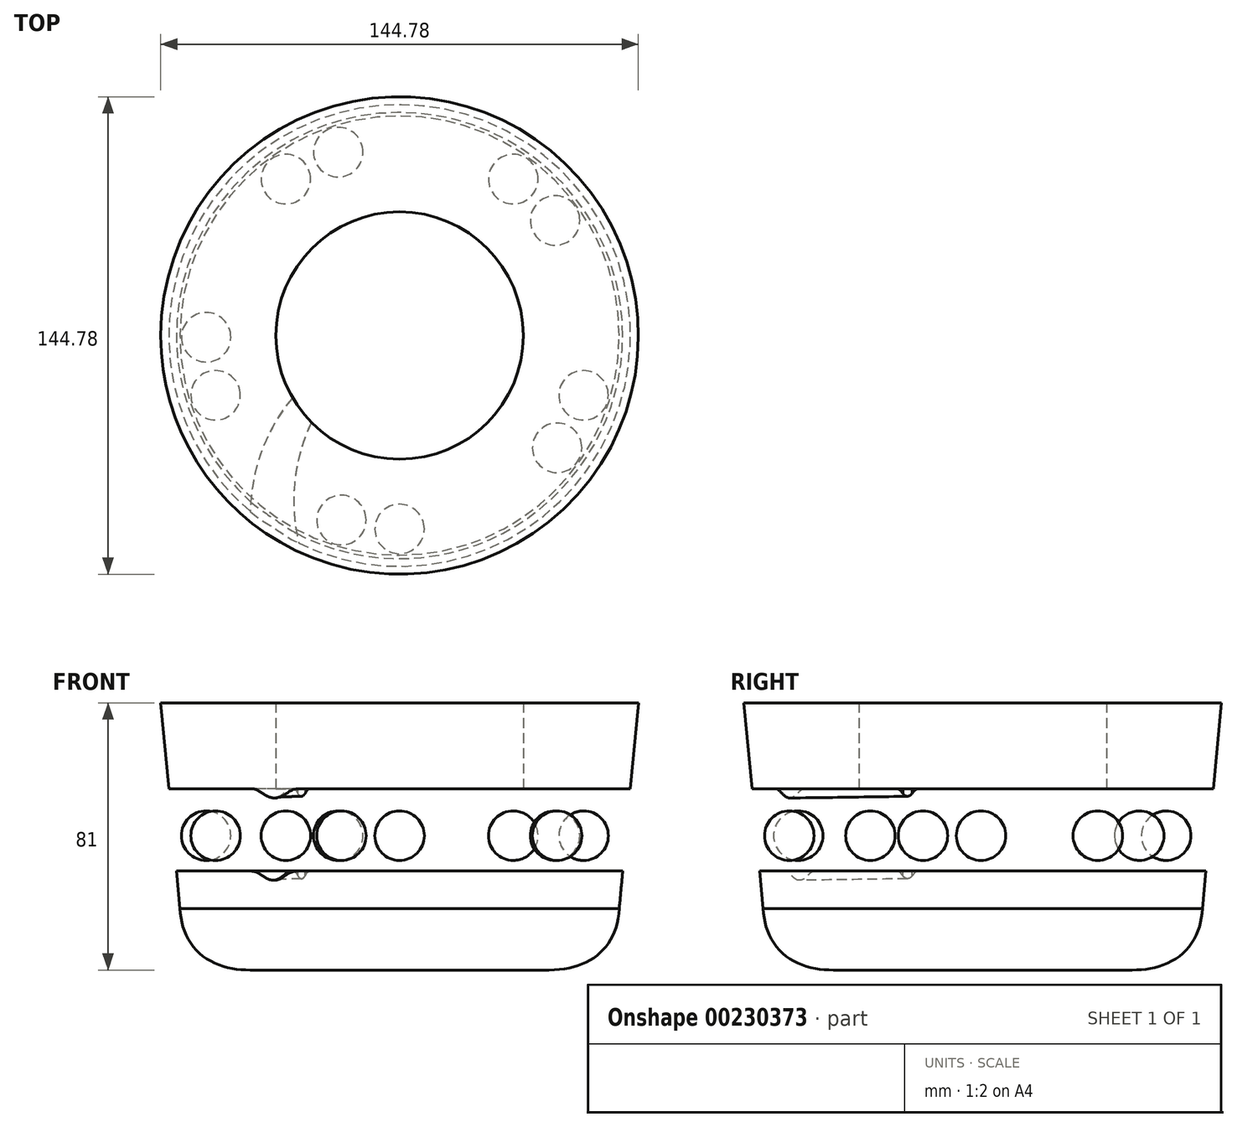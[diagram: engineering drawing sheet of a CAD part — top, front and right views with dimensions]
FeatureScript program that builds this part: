
annotation { "Feature Type Name" : "Feature", "Feature Type Description" : "" }
export const myFeature = defineFeature(function(context is Context, id is Id, definition is map)
    precondition{}
    {
        {
            var Q0;
            Q0=qCreatedBy(makeId("Top.planeOp"),FACE);
            var sketch = newSketch(context, id + "F0", { "sketchPlane" : qUnion([Q0])});
            skCircle(sketch, "E0", {"center": v(0, 0) * mm, "radius": 75 * mm});
            skSolve(sketch);
        }
        {
            var Q0;
            Q0 = qSketchRegion(id + "F0", true);
            extrude(context, id + "F1", {"entities" : qUnion([Q0]), "depth" : 30 * mm, "offsetDistance" : 25 * mm});
        }
        {
            var Q0;
            Q0=makeQuery(id+"F1.opExtrude","CAP_FACE",FACE,{"disambiguationData":[OSD([sQuery(id+"F0.wireOp",EDGE,"E0")])],"isStart":false});
            var sketch = newSketch(context, id + "F2", { "sketchPlane" : qUnion([Q0])});
            skCircle(sketch, "E1", {"center": v(0, 0) * mm, "radius": 37.5 * mm});
            skSolve(sketch);
        }
        {
            var Q0;
            Q0=makeQuery(id+"F2.imprint","IMPRINT",FACE,{"disambiguationData":[TD([[makeQuery(id+"F2.imprint","IMPRINT",EDGE,{"derivedFrom":sQuery(id+"F2.wireOp",EDGE,"E1")}),1.0]])]});
            extrude(context, id + "F3", {"entities" : qUnion([Q0]), "operationType" : NewBodyOperationType.REMOVE, "oppositeDirection" : true, "depth" : 30 * mm, "offsetDistance" : 25 * mm});
        }
        {
            var Q0;
            Q0=makeQuery(id+"F1.opExtrude","CAP_FACE",FACE,{"disambiguationData":[OSD([sQuery(id+"F0.wireOp",EDGE,"E0")])],"isStart":false});
            var sketch = newSketch(context, id + "F4", { "sketchPlane" : qUnion([Q0])});
            skCircle(sketch, "E2", {"center": v(0, 0) * mm, "radius": 100 * mm});
            skCircle(sketch, "E3", {"center": v(0, 0) * mm, "radius": 37.75 * mm});
            skArc(sketch, "E4", {"start": v(-26.84, -26.55) * mm, "mid": v(-28.75, -68.88) * mm, "end": v(0, -100) * mm});
            skPoint(sketch, "E5", {"position": v(-26.84, -26.55) * mm});
            skArc(sketch, "E6.1.0", {"start": v(0, 0) * mm, "mid": v(-18.64, -56.4) * mm, "end": v(24.87, -96.86) * mm});
            skArc(sketch, "E6.2.0", {"start": v(0, 0) * mm, "mid": v(-4.03, -59.27) * mm, "end": v(48.18, -87.63) * mm});
            skArc(sketch, "E6.3.0", {"start": v(0, 0) * mm, "mid": v(10.84, -58.41) * mm, "end": v(68.45, -72.9) * mm});
            skArc(sketch, "E6.4.0", {"start": v(0, 0) * mm, "mid": v(25.02, -53.88) * mm, "end": v(84.43, -53.58) * mm});
            skArc(sketch, "E6.5.0", {"start": v(0, 0) * mm, "mid": v(37.64, -45.97) * mm, "end": v(95.1, -30.9) * mm});
            skArc(sketch, "E6.6.0", {"start": v(0, 0) * mm, "mid": v(47.89, -35.16) * mm, "end": v(99.8, -6.28) * mm});
            skArc(sketch, "E6.7.0", {"start": v(0, 0) * mm, "mid": v(55.13, -22.15) * mm, "end": v(98.23, 18.74) * mm});
            skArc(sketch, "E6.8.0", {"start": v(0, 0) * mm, "mid": v(58.9, -7.74) * mm, "end": v(90.48, 42.58) * mm});
            skArc(sketch, "E6.9.0", {"start": v(0, 0) * mm, "mid": v(58.98, 7.15) * mm, "end": v(77.05, 63.74) * mm});
            skArc(sketch, "E6.10.0", {"start": v(0, 0) * mm, "mid": v(55.35, 21.6) * mm, "end": v(58.78, 80.9) * mm});
            skArc(sketch, "E6.11.0", {"start": v(0, 0) * mm, "mid": v(48.24, 34.68) * mm, "end": v(36.81, 92.98) * mm});
            skArc(sketch, "E6.12.0", {"start": v(0, 0) * mm, "mid": v(38.1, 45.58) * mm, "end": v(12.53, 99.21) * mm});
            skArc(sketch, "E6.13.0", {"start": v(0, 0) * mm, "mid": v(25.57, 53.63) * mm, "end": v(-12.53, 99.21) * mm});
            skArc(sketch, "E6.14.0", {"start": v(0, 0) * mm, "mid": v(11.43, 58.3) * mm, "end": v(-36.81, 92.98) * mm});
            skArc(sketch, "E6.15.0", {"start": v(0, 0) * mm, "mid": v(-3.43, 59.31) * mm, "end": v(-58.78, 80.9) * mm});
            skArc(sketch, "E6.16.0", {"start": v(0, 0) * mm, "mid": v(-18.07, 56.6) * mm, "end": v(-77.05, 63.74) * mm});
            skArc(sketch, "E6.17.0", {"start": v(0, 0) * mm, "mid": v(-31.58, 50.32) * mm, "end": v(-90.48, 42.58) * mm});
            skArc(sketch, "E6.18.0", {"start": v(0, 0) * mm, "mid": v(-43.1, 40.89) * mm, "end": v(-98.23, 18.74) * mm});
            skArc(sketch, "E6.19.0", {"start": v(0, 0) * mm, "mid": v(-51.92, 28.88) * mm, "end": v(-99.8, -6.28) * mm});
            skArc(sketch, "E6.20.0", {"start": v(0, 0) * mm, "mid": v(-57.47, 15.07) * mm, "end": v(-95.1, -30.9) * mm});
            skArc(sketch, "E6.21.0", {"start": v(0, 0) * mm, "mid": v(-59.4, 0.3) * mm, "end": v(-84.43, -53.58) * mm});
            skArc(sketch, "E6.22.0", {"start": v(0, 0) * mm, "mid": v(-57.62, -14.48) * mm, "end": v(-68.45, -72.9) * mm});
            skArc(sketch, "E6.23.0", {"start": v(0, 0) * mm, "mid": v(-52.2, -28.36) * mm, "end": v(-48.18, -87.63) * mm});
            skArc(sketch, "E6.24.0", {"start": v(-32.6, -19.04) * mm, "mid": v(-44.97, -59.56) * mm, "end": v(-24.87, -96.86) * mm});
            skLineSegment(sketch, "E7", {"start": v(0, -100) * mm, "end": v(-24.87, -96.86) * mm});
            skPoint(sketch, "E8", {"position": v(-32.6, -19.04) * mm});
            skLineSegment(sketch, "E9", {"start": v(-32.6, -19.04) * mm, "end": v(-26.84, -26.55) * mm});
            skPoint(sketch, "E10", {"position": v(-29.72, -22.8) * mm});
            skSolve(sketch);
        }
        {
            var Q0;
            Q0=makeQuery(id+"F1.opExtrude","SWEPT_BODY",BODY,{"disambiguationData":[OSD([sQuery(id+"F0.wireOp",EDGE,"E0")])]});
            var Q1;
            Q1=qCreatedBy(makeId("Top.planeOp"),FACE);
            mirror(context, id + "F5", {"entities" : qUnion([Q0]), "mirrorPlane" : qUnion([Q1])});
        }
        {
            var Q0;
            Q0=sQuery(id+"F4.wireOp",EDGE,"E7");
            cPlane(context, id + "F6", {"entities" : qUnion([Q0]), "cplaneType" : CPlaneType.LINE_ANGLE, "offset" : 25 * mm, "angle" : 0 * degree, "width" : 150 * mm, "height" : 150 * mm});
        }
        {
            var Q0;
            Q0=qCreatedBy(id+"F6.planeOp",FACE);
            var sketch = newSketch(context, id + "F7", { "sketchPlane" : qUnion([Q0])});
            skPoint(sketch, "E11.0", {"position": v(-12.53, 30) * mm});
            skPoint(sketch, "E12.0", {"position": v(12.53, 30) * mm});
            skPoint(sketch, "E13.0", {"position": v(0, 30) * mm});
            skFitSpline(sketch, "E14", {"points": [v(-12.53, 30) * mm, v(-5.15, 27.51) * mm, v(0, 26.47) * mm, v(5.15, 27.51) * mm, v(12.53, 30) * mm], "startDerivative": vector(33.53, 0) * mm, "endDerivative": vector(33.53, 0) * mm});
            skLineSegment(sketch, "E15", {"start": v(-12.53, 30) * mm, "end": v(12.53, 30) * mm});
            skLineSegment(sketch, "E16", {"start": v(0, 30) * mm, "end": v(0, 26.47) * mm, "construction": true});
            skSolve(sketch);
        }
        {
            var Q0;
            Q0=sQuery(id+"F4.wireOp",EDGE,"E9");
            cPlane(context, id + "F8", {"entities" : qUnion([Q0]), "cplaneType" : CPlaneType.LINE_ANGLE, "offset" : 25 * mm, "angle" : 90 * degree, "width" : 150 * mm, "height" : 150 * mm});
        }
        {
            var Q0;
            Q0=qCreatedBy(id+"F8.planeOp",FACE);
            var sketch = newSketch(context, id + "F9", { "sketchPlane" : qUnion([Q0])});
            skPoint(sketch, "E17.0", {"position": v(4.73, 30) * mm});
            skPoint(sketch, "E18.0", {"position": v(0, 30) * mm});
            skPoint(sketch, "E19.0", {"position": v(-4.73, 30) * mm});
            skFitSpline(sketch, "E20", {"points": [v(4.73, 30) * mm, v(2.06, 28.8) * mm, v(0, 27.68) * mm, v(-2.06, 28.8) * mm, v(-4.73, 30) * mm], "startDerivative": vector(-21.02, 0) * mm, "endDerivative": vector(-21.02, 0) * mm});
            skLineSegment(sketch, "E21", {"start": v(4.73, 30) * mm, "end": v(-4.73, 30) * mm});
            skLineSegment(sketch, "E22", {"start": v(0, 30) * mm, "end": v(0, 27.68) * mm, "construction": true});
            skSolve(sketch);
        }
        {
            var Q1;
            Q1 = qSketchRegion(id + "F7", true);
            var Q2;
            Q2 = qSketchRegion(id + "F9", true);
            var Q3;
            Q3=sQuery(id+"F4.wireOp",EDGE,"E6.24.0");
            var Q4;
            Q4=sQuery(id+"F4.wireOp",EDGE,"E4");
            loft(context, id + "F10", {"operationType" : NewBodyOperationType.REMOVE, "addGuides" : true, "sheetProfilesArray" : [{ "sheetProfileEntities" : qUnion([Q1]) }, { "sheetProfileEntities" : qUnion([Q2]) }], "guidesArray" : [{ "guideEntities" : qUnion([Q3]), "guideDerivativeType" : LoftGuideDerivativeType.DEFAULT, "guideDerivativeMagnitude" : 1 }, { "guideEntities" : qUnion([Q4]), "guideDerivativeType" : LoftGuideDerivativeType.DEFAULT, "guideDerivativeMagnitude" : 1 }]});
        }
        {
            var Q0;
            Q0=makeQuery(id+"F5.opPattern","COPY",BODY,{"derivedFrom":makeQuery(id+"F1.opExtrude","SWEPT_BODY",BODY,{"disambiguationData":[OSD([sQuery(id+"F0.wireOp",EDGE,"E0")])]}),"instanceName":"1"});
            var Q1;
            Q1=qCreatedBy(makeId("Top.planeOp"),FACE);
            transform(context, id + "F11", {"entities" : qUnion([Q0]), "transformType" : TransformType.TRANSLATION_DISTANCE, "transformDirection" : qUnion([Q1]), "distance" : 56 * mm, "makeCopy" : false});
        }
        {
            var Q0;
            Q0=makeQuery(id+"F1.opExtrude","SWEPT_BODY",BODY,{"disambiguationData":[OSD([sQuery(id+"F0.wireOp",EDGE,"E0")])]});
            var Q1;
            Q1=makeQuery(id+"F5.opPattern","COPY",BODY,{"derivedFrom":makeQuery(id+"F1.opExtrude","SWEPT_BODY",BODY,{"disambiguationData":[OSD([sQuery(id+"F0.wireOp",EDGE,"E0")])]}),"instanceName":"1"});
            booleanBodies(context, id + "F12", {"operationType" : BooleanOperationType.SUBTRACTION, "tools" : qUnion([Q0]), "targets" : qUnion([Q1]), "keepTools" : true});
        }
        {
            var Q0;
            Q0=makeQuery(id+"F5.opPattern","COPY",BODY,{"derivedFrom":makeQuery(id+"F1.opExtrude","SWEPT_BODY",BODY,{"disambiguationData":[OSD([sQuery(id+"F0.wireOp",EDGE,"E0")])]}),"instanceName":"1"});
            var Q1;
            Q1=qCreatedBy(makeId("Top.planeOp"),FACE);
            transform(context, id + "F13", {"entities" : qUnion([Q0]), "transformType" : TransformType.TRANSLATION_DISTANCE, "transformDirection" : qUnion([Q1]), "distance" : 25 * mm, "makeCopy" : false});
        }
        {
            var Q0;
            Q0=qCreatedBy(makeId("Top.planeOp"),FACE);
            var sketch = newSketch(context, id + "F14", { "sketchPlane" : qUnion([Q0])});
            skCircle(sketch, "E23", {"center": v(0, 0) * mm, "radius": 65 * mm});
            skSolve(sketch);
        }
        {
            var Q0;
            Q0=makeQuery(id+"F5.opPattern","COPY",FACE,{"derivedFrom":makeQuery(id+"F1.opExtrude","CAP_FACE",FACE,{"disambiguationData":[OSD([sQuery(id+"F0.wireOp",EDGE,"E0")])],"isStart":true}),"instanceName":"1"});
            var sketch = newSketch(context, id + "F15", { "sketchPlane" : qUnion([Q0])});
            skCircle(sketch, "E24", {"center": v(0, 0) * mm, "radius": 72.5 * mm});
            skSolve(sketch);
        }
        {
            var Q1;
            Q1=makeQuery(id+"F14.imprint","IMPRINT",FACE,{"disambiguationData":[TD([[makeQuery(id+"F14.imprint","IMPRINT",EDGE,{"derivedFrom":sQuery(id+"F14.wireOp",EDGE,"E23")}),1.0]])]});
            var Q2;
            Q2 = qSketchRegion(id + "F15", true);
            loft(context, id + "F16", {"operationType" : NewBodyOperationType.INTERSECT, "sheetProfilesArray" : [{ "sheetProfileEntities" : qUnion([Q1]) }, { "sheetProfileEntities" : qUnion([Q2]) }]});
        }
        {
            var Q0;
            Q0=qCreatedBy(makeId("Right.planeOp"),FACE);
            var sketch = newSketch(context, id + "F17", { "sketchPlane" : qUnion([Q0])});
            skFitSpline(sketch, "E25", {"points": [v(-45.31, 0) * mm, v(-66.57, 18.58) * mm], "startDerivative": vector(-37.05, 0) * mm, "endDerivative": vector(-1.82, 35.84) * mm});
            skLineSegment(sketch, "E26", {"start": v(-66.57, 18.58) * mm, "end": v(-72.44, 81.55) * mm});
            skLineSegment(sketch, "E27", {"start": v(-72.44, 81.55) * mm, "end": v(0, 81.55) * mm});
            skLineSegment(sketch, "E28", {"start": v(0, 81.55) * mm, "end": v(0, 0) * mm});
            skLineSegment(sketch, "E29", {"start": v(0, 0) * mm, "end": v(-45.31, 0) * mm});
            skSolve(sketch);
        }
        {
            var Q0;
            Q0=makeQuery(id+"F17.imprint","IMPRINT",FACE,{"disambiguationData":[TD([[makeQuery(id+"F17.imprint","IMPRINT",EDGE,{"derivedFrom":sQuery(id+"F17.wireOp",EDGE,"E25")}),-1.0]])]});
            var Q1;
            Q1=sQuery(id+"F17.wireOp",EDGE,"E28");
            revolve(context, id + "F18", {"operationType" : NewBodyOperationType.INTERSECT, "surfaceOperationType" : NewSurfaceOperationType.NEW, "entities" : qUnion([Q0]), "axis" : qUnion([Q1]), "revolveType" : RevolveType.FULL});
        }
        {
            var Q0;
            Q0 = qSketchRegion(id + "F2", true);
            var Q1;
            Q1=qCreatedBy(makeId("Origin.pointOp"),VERTEX);
            extrude(context, id + "F19", {"entities" : qUnion([Q0]), "operationType" : NewBodyOperationType.ADD, "endBound" : BoundingType.UP_TO_VERTEX, "oppositeDirection" : true, "depth" : 25 * mm, "endBoundEntityVertex" : qUnion([Q1]), "offsetDistance" : 25 * mm});
        }
        {
            var Q0;
            Q0=qCreatedBy(makeId("Right.planeOp"),FACE);
            var sketch = newSketch(context, id + "F20", { "sketchPlane" : qUnion([Q0])});
            skArc(sketch, "E30", {"start": v(-58.65, 48.23) * mm, "mid": v(-66.15, 40.73) * mm, "end": v(-58.65, 33.23) * mm});
            skLineSegment(sketch, "E31", {"start": v(-58.65, 33.23) * mm, "end": v(-58.65, 48.23) * mm});
            skSolve(sketch);
        }
        {
            var Q0;
            Q0=makeQuery(id+"F20.imprint","IMPRINT",FACE,{"disambiguationData":[TD([[makeQuery(id+"F20.imprint","IMPRINT",EDGE,{"derivedFrom":sQuery(id+"F20.wireOp",EDGE,"E30")}),1.0]])]});
            var Q1;
            Q1=sQuery(id+"F20.wireOp",EDGE,"E31");
            revolve(context, id + "F21", {"surfaceOperationType" : NewSurfaceOperationType.NEW, "entities" : qUnion([Q0]), "axis" : qUnion([Q1]), "revolveType" : RevolveType.FULL});
        }
        {
            var Q0;
            Q0=makeQuery(id+"F21.opRevolve","SWEPT_BODY",BODY,{"disambiguationData":[OSD([sQuery(id+"F20.wireOp",EDGE,"E30"),sQuery(id+"F20.wireOp",EDGE,"E31")])]});
            var Q1;
            Q1=sQuery(id+"F4.wireOp",EDGE,"E3");
            transform(context, id + "F22", {"entities" : qUnion([Q0]), "transformType" : TransformType.ROTATION, "transformAxis" : qUnion([Q1]), "angle" : 17.5 * degree, "oppositeDirection" : true, "makeCopy" : true});
        }
        {
            var Q0;
            Q0=makeQuery(id+"F21.opRevolve","SWEPT_BODY",BODY,{"disambiguationData":[OSD([sQuery(id+"F20.wireOp",EDGE,"E30"),sQuery(id+"F20.wireOp",EDGE,"E31")])]});
            var Q1;
            Q1=makeQuery(id+"F22.opPattern","COPY",BODY,{"derivedFrom":makeQuery(id+"F21.opRevolve","SWEPT_BODY",BODY,{"disambiguationData":[OSD([sQuery(id+"F20.wireOp",EDGE,"E30"),sQuery(id+"F20.wireOp",EDGE,"E31")])]}),"instanceName":"1"});
            var Q2;
            Q2=sQuery(id+"F4.wireOp",EDGE,"E3");
            circularPattern(context, id + "F23", {"entities" : qUnion([Q0, Q1]), "axis" : qUnion([Q2]), "angle" : 360 * degree, "instanceCount" : 5, "equalSpace" : true});
        }
    });
